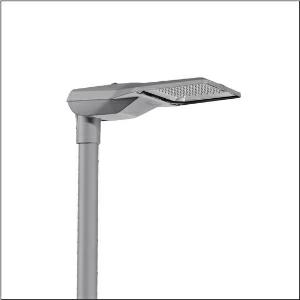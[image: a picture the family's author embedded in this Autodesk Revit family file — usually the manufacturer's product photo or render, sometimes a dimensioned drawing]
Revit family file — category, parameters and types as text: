
# Revit family: streetlight_sl_21_midi___st1_0ab_5xe3m33s08lb_591c
name_source: partatom
category: Lighting Fixtures
units: mm (PartAtom-declared; Revit-internal decimal feet)

## family parameters
Cut with Voids When Loaded = No
Host = Face
Light Source = No
Part Type = Normal
Room Calculation Point = No
Round Connector Dimension = Use Diameter
Shared = No

## types (1)
- --- (1 x LED, 12620 lm, 98.3 W, 3000K)
    Apparent Load = 98 VA
    CIE Flux Codes = 38 73 97 100 100
    Color Rendering = 70
    Color Temperature = 3000K
    Default Elevation = 1800 mm
    Description = Streetlight SL 21 midi, mast luminaire, primary light control with lens, of PMMA, primary optical cover: cover, of toughened safety glass, transparent, light distribution: ST1.0aB, light emission: direct distribution, primary light characteristic: asymmetric, installation type: side-entry, post-top, LED, High Power LED, rated luminous flux: 12.620lm, luminous efficacy: 128lm/W, light colour: 730, colour temperature: 3000K, control: flexible luminous flux parameterisation, time-dependent luminous flux control, constant luminous flux control, overheat protection, presetting dimming logarithmic, mains connection: 230..240V, AC, 50/60Hz, start of lifetime: 98W, end of service life: 101W, reduction: 45W, luminaire housing, of diecast aluminium, powder-coated, Siteco® metallic grey (DB 702S), corrosivity category C5 mid according to DIN EN ISO 12944, please order mast flange separately, inclination adjustable: 0°, 5°, 10°, 15°, sealing non-destructively replaceable, multi-level sealing system, length: 644mm, width: 335mm, height: 110mm, mast flange for spigot size: 42mm (side-entry): 5XC10008XM4, 60/48mm (side-entry/post-top): 5XC10108XM2, 76/60mm (side-entry/post-top): 5XC10108XM1, Smart Interface above, protection rating (complete): IP66, insulation class (complete): insulation class II (safety insulation), certification: CE, ENEC, ENEC+, VDE, impact resistance: IK09, permissible operating ambient temperature for outdoor applications: -40..+50°C, standard-compliant lighting for roads and squares, packaging unit: 1 piece

Light Distribution: ST1.0aB
    Height = 111 mm
    Lamp = 1 x LED
    Lamp Light Flux = 12620 lm
    Lamp Power = 98.3 W
    Lamp count = 1
    Length = 644 mm
    Luminous efficacy = 128 lm/W
    Manufacturer = Siteco
    ModVariant = No
    Model = 5XE3M33S08LB
    Number of Poles = 1
    OnlyDefault = Yes
    Power Factor = 1
    Product Name = Streetlight SL 21 midi | ST1.0aB
    Product group = mast luminaire | pylon top
    ProductGroupID = 6100
    Protection Class = Protection class II
    Protection Degree = IP 66
    RLX_Detail_Level = 1
    RLX_Emergency_Light_Flux = 0 lm
    RLX_Emergency_Type = 0
    RLX_Emergency_Type_DB = No
    RlxData = <blob elided: 90737 chars, md5=bbeed8ba>
    Socket = socket
    Standby Power = 0 W
    System Light Flux = 12620 lm
    System Power = 98 W
    Type Comments = factory setting: luminous flux: 100 % | dim-lin: 254 | 1020 mA
    Type Image = l_1004302.jpg
    URL = http://relux.com
    VarID = @adj_134443
    Voltage = 0 V
    Weight = 0.00 kg
    Width = 336 mm

## geometry (parser evidence)
native form markers: Blend x4, Sweep x9
no freeform markers — native parametric forms only
